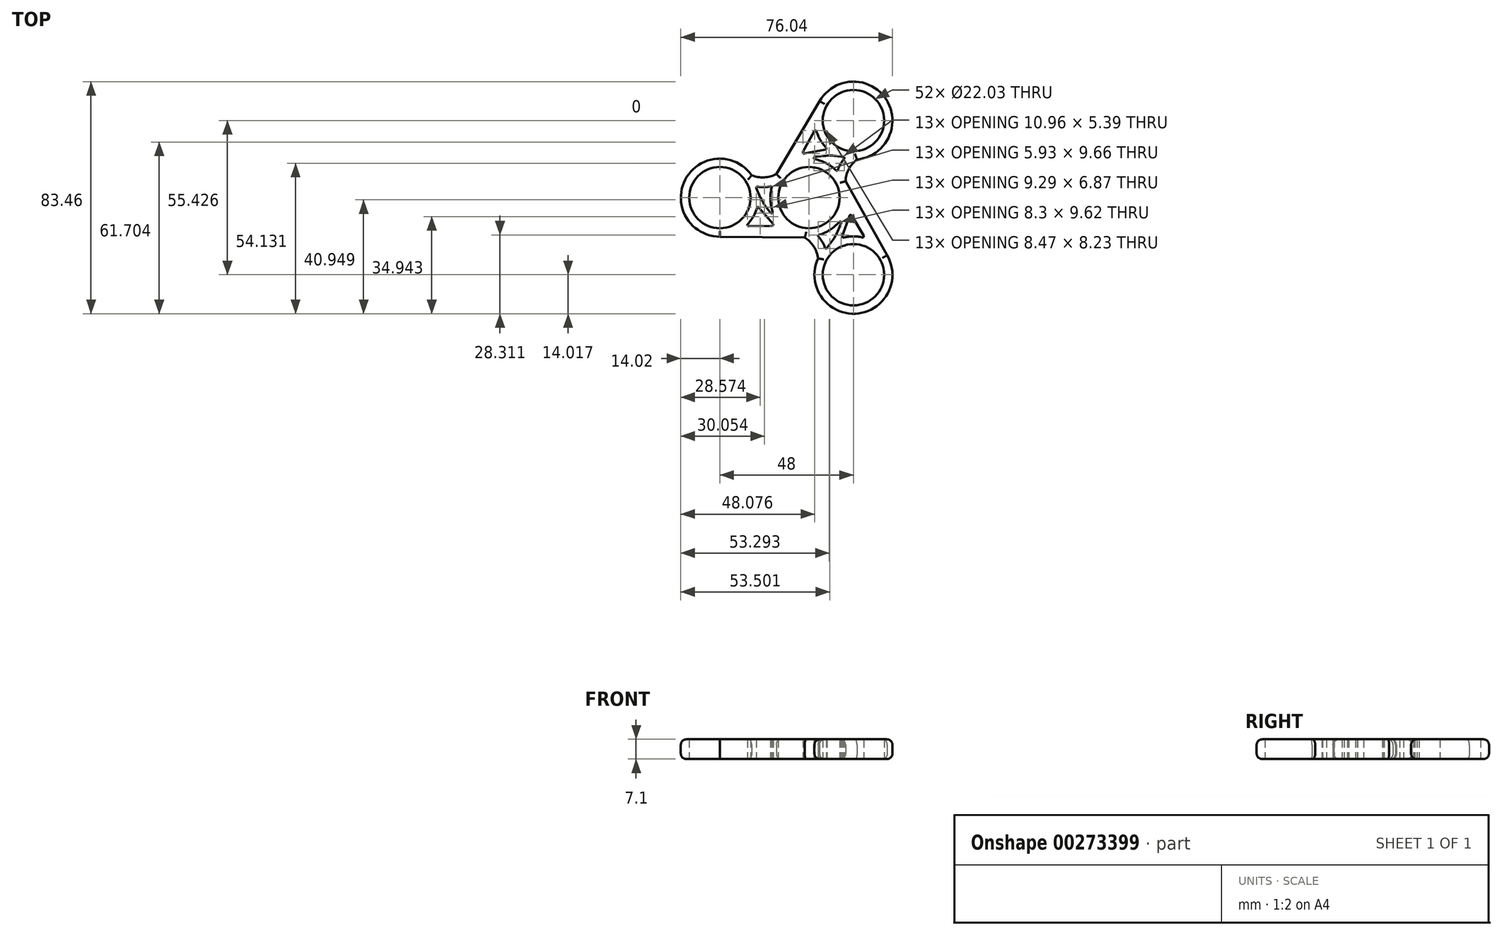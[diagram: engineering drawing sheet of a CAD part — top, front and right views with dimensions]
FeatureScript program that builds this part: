
annotation { "Feature Type Name" : "Feature", "Feature Type Description" : "" }
export const myFeature = defineFeature(function(context is Context, id is Id, definition is map)
    precondition{}
    {
        {
            var Q0;
            Q0=qCreatedBy(makeId("Top.planeOp"),FACE);
            var sketch = newSketch(context, id + "F0", { "sketchPlane" : qUnion([Q0])});
            skCircle(sketch, "E0", {"center": v(0, 0) * mm, "radius": 11.02 * mm});
            skCircle(sketch, "E1", {"center": v(16, 27.71) * mm, "radius": 11.02 * mm});
            skLineSegment(sketch, "E2", {"start": v(0, 0) * mm, "end": v(16, 27.71) * mm, "construction": true});
            skArc(sketch, "E3", {"start": v(17.28, 13.76) * mm, "mid": v(27.8, 35.27) * mm, "end": v(3.86, 34.72) * mm});
            skLineSegment(sketch, "E4", {"start": v(16, 27.71) * mm, "end": v(3.86, 34.72) * mm, "construction": true});
            skPoint(sketch, "E5.visualSharp", {"position": v(9, 15.58) * mm});
            skLineSegment(sketch, "E6", {"start": v(16, 27.71) * mm, "end": v(28.14, 20.7) * mm, "construction": true});
            skArc(sketch, "E7", {"start": v(2.75, 23.79) * mm, "mid": v(4.1, 20.69) * mm, "end": v(6.17, 18) * mm});
            skPoint(sketch, "E8.center", {"position": v(-0.23, 0.06) * mm});
            skLineSegment(sketch, "E9", {"start": v(5.94, 17.3) * mm, "end": v(-1.68, 15.87) * mm});
            skPoint(sketch, "E10.orphan", {"position": v(9.2, 15.94) * mm});
            skPoint(sketch, "E11.1.5", {"position": v(0.06, -0.23) * mm});
            skPoint(sketch, "E11.2.5", {"position": v(0.17, 0.17) * mm});
            skLineSegment(sketch, "E12", {"start": v(1.98, 23.87) * mm, "end": v(-2.13, 16.49) * mm});
            skArc(sketch, "E13", {"start": v(12.66, 13.98) * mm, "mid": v(11.36, 12.1) * mm, "end": v(10.44, 10) * mm});
            skArc(sketch, "E14", {"start": v(9.74, 9.82) * mm, "mid": v(6.22, 12.36) * mm, "end": v(2.13, 13.8) * mm});
            skPoint(sketch, "E15.orphan", {"position": v(2.3, 25.96) * mm});
            skArc(sketch, "E16.filletArc", {"start": v(-2.13, 16.49) * mm, "mid": v(-2.1, 16.03) * mm, "end": v(-1.68, 15.87) * mm});
            skPoint(sketch, "E17.visualSharp", {"position": v(10.24, 9.32) * mm});
            skArc(sketch, "E17.filletArc", {"start": v(9.74, 9.82) * mm, "mid": v(10.14, 9.72) * mm, "end": v(10.44, 10) * mm});
            skPoint(sketch, "E18.visualSharp", {"position": v(13.18, 14.57) * mm});
            skArc(sketch, "E18.filletArc", {"start": v(12.66, 13.98) * mm, "mid": v(12.73, 14.4) * mm, "end": v(12.38, 14.67) * mm});
            skArc(sketch, "E19.filletArc", {"start": v(2.16, 14.64) * mm, "mid": v(1.8, 14.24) * mm, "end": v(2.13, 13.8) * mm});
            skPoint(sketch, "E20.visualSharp", {"position": v(6.76, 17.44) * mm});
            skArc(sketch, "E20.filletArc", {"start": v(5.94, 17.3) * mm, "mid": v(6.27, 17.58) * mm, "end": v(6.17, 18) * mm});
            skPoint(sketch, "E21.visualSharp", {"position": v(2.5, 24.8) * mm});
            skArc(sketch, "E21.filletArc", {"start": v(2.75, 23.79) * mm, "mid": v(2.4, 24.09) * mm, "end": v(1.98, 23.87) * mm});
            skArc(sketch, "E22", {"start": v(12.38, 14.67) * mm, "mid": v(7.27, 15.1) * mm, "end": v(2.16, 14.64) * mm});
            skArc(sketch, "E23", {"start": v(17.28, 13.76) * mm, "mid": v(14.34, 10.27) * mm, "end": v(13.18, 5.86) * mm});
            skLineSegment(sketch, "E24.1.1", {"start": v(-11.67, 8.49) * mm, "end": v(3.86, 34.72) * mm});
            skArc(sketch, "E25.1.0", {"start": v(-20.55, 8.08) * mm, "mid": v(-44.44, 6.45) * mm, "end": v(-32, -14.01) * mm});
            skPoint(sketch, "E25.1.1", {"position": v(-23.63, -11) * mm});
            skPoint(sketch, "E25.1.2", {"position": v(-13.2, 4.2) * mm});
            skLineSegment(sketch, "E25.1.3", {"start": v(-1.51, -14.35) * mm, "end": v(-32, -14.01) * mm});
            skArc(sketch, "E25.1.4", {"start": v(-20.55, 8.08) * mm, "mid": v(-16.06, 7.28) * mm, "end": v(-11.67, 8.49) * mm});
            skCircle(sketch, "E25.1.5", {"center": v(-32, 0) * mm, "radius": 11.02 * mm});
            skPoint(sketch, "E25.1.6", {"position": v(-19.2, 4.13) * mm});
            skPoint(sketch, "E25.1.7", {"position": v(-17.98, 0) * mm});
            skArc(sketch, "E25.1.8", {"start": v(-21.98, -9.5) * mm, "mid": v(-19.97, -6.79) * mm, "end": v(-18.68, -3.66) * mm});
            skLineSegment(sketch, "E25.1.9", {"start": v(-21.66, -10.22) * mm, "end": v(-13.22, -10.09) * mm});
            skArc(sketch, "E25.1.10", {"start": v(-13.38, 3.53) * mm, "mid": v(-13.82, -0.8) * mm, "end": v(-13.02, -5.06) * mm});
            skArc(sketch, "E25.1.11", {"start": v(-18.9, 3.39) * mm, "mid": v(-16.71, -1.25) * mm, "end": v(-13.76, -5.45) * mm});
            skPoint(sketch, "E25.1.12", {"position": v(-18.4, 0) * mm});
            skLineSegment(sketch, "E25.1.13", {"start": v(-17.95, -3.5) * mm, "end": v(-12.9, -9.39) * mm});
            skPoint(sketch, "E25.1.14", {"position": v(-18.49, -2.87) * mm});
            skPoint(sketch, "E25.1.15", {"position": v(-22.73, -10.24) * mm});
            skArc(sketch, "E25.1.16", {"start": v(-18.44, 3.97) * mm, "mid": v(-18.84, 3.82) * mm, "end": v(-18.9, 3.39) * mm});
            skArc(sketch, "E25.1.17", {"start": v(-18.44, 3.97) * mm, "mid": v(-16.15, 3.8) * mm, "end": v(-13.88, 4.04) * mm});
            skArc(sketch, "E25.1.18", {"start": v(-13.22, -10.09) * mm, "mid": v(-12.84, -9.84) * mm, "end": v(-12.9, -9.39) * mm});
            skArc(sketch, "E25.1.19", {"start": v(-21.98, -9.5) * mm, "mid": v(-22.06, -9.97) * mm, "end": v(-21.66, -10.22) * mm});
            skArc(sketch, "E25.1.20", {"start": v(-13.38, 3.53) * mm, "mid": v(-13.48, 3.92) * mm, "end": v(-13.88, 4.04) * mm});
            skArc(sketch, "E25.1.21", {"start": v(-13.76, -5.45) * mm, "mid": v(-13.23, -5.57) * mm, "end": v(-13.02, -5.06) * mm});
            skArc(sketch, "E25.1.22", {"start": v(-17.95, -3.5) * mm, "mid": v(-18.36, -3.36) * mm, "end": v(-18.68, -3.66) * mm});
            skArc(sketch, "E25.2.0", {"start": v(3.28, -21.84) * mm, "mid": v(16.64, -41.71) * mm, "end": v(28.14, -20.7) * mm});
            skPoint(sketch, "E25.2.1", {"position": v(21.34, -14.97) * mm});
            skPoint(sketch, "E25.2.2", {"position": v(2.95, -13.53) * mm});
            skLineSegment(sketch, "E25.2.3", {"start": v(13.18, 5.86) * mm, "end": v(28.14, -20.7) * mm});
            skArc(sketch, "E25.2.4", {"start": v(3.28, -21.84) * mm, "mid": v(1.72, -17.55) * mm, "end": v(-1.51, -14.35) * mm});
            skCircle(sketch, "E25.2.5", {"center": v(16, -27.71) * mm, "radius": 11.02 * mm});
            skPoint(sketch, "E25.2.6", {"position": v(6.03, -18.7) * mm});
            skPoint(sketch, "E25.2.7", {"position": v(9, -15.58) * mm});
            skArc(sketch, "E25.2.8", {"start": v(19.22, -14.28) * mm, "mid": v(15.86, -13.9) * mm, "end": v(12.51, -14.35) * mm});
            skLineSegment(sketch, "E25.2.9", {"start": v(19.68, -13.65) * mm, "end": v(15.34, -6.4) * mm});
            skArc(sketch, "E25.2.10", {"start": v(3.64, -13.35) * mm, "mid": v(7.6, -11.57) * mm, "end": v(10.9, -8.75) * mm});
            skArc(sketch, "E25.2.11", {"start": v(6.52, -18.06) * mm, "mid": v(9.44, -13.85) * mm, "end": v(11.6, -9.2) * mm});
            skPoint(sketch, "E25.2.12", {"position": v(9.2, -15.94) * mm});
            skLineSegment(sketch, "E25.2.13", {"start": v(12, -13.8) * mm, "end": v(14.58, -6.48) * mm});
            skPoint(sketch, "E25.2.14", {"position": v(11.73, -14.57) * mm});
            skPoint(sketch, "E25.2.15", {"position": v(20.23, -14.56) * mm});
            skArc(sketch, "E25.2.16", {"start": v(5.78, -17.95) * mm, "mid": v(6.11, -18.23) * mm, "end": v(6.52, -18.06) * mm});
            skArc(sketch, "E25.2.17", {"start": v(5.78, -17.95) * mm, "mid": v(4.8, -15.88) * mm, "end": v(3.44, -14.04) * mm});
            skArc(sketch, "E25.2.18", {"start": v(15.34, -6.4) * mm, "mid": v(14.94, -6.2) * mm, "end": v(14.58, -6.48) * mm});
            skArc(sketch, "E25.2.19", {"start": v(19.22, -14.28) * mm, "mid": v(19.66, -14.12) * mm, "end": v(19.68, -13.65) * mm});
            skArc(sketch, "E25.2.20", {"start": v(3.64, -13.35) * mm, "mid": v(3.35, -13.64) * mm, "end": v(3.44, -14.04) * mm});
            skArc(sketch, "E25.2.21", {"start": v(11.6, -9.2) * mm, "mid": v(11.43, -8.67) * mm, "end": v(10.9, -8.75) * mm});
            skArc(sketch, "E25.2.22", {"start": v(12, -13.8) * mm, "mid": v(12.1, -14.22) * mm, "end": v(12.51, -14.35) * mm});
            skLineSegment(sketch, "E26", {"start": v(30.02, 27.71) * mm, "end": v(30.02, -27.71) * mm, "construction": true});
            skCircle(sketch, "E27", {"center": v(0, 0) * mm, "radius": 45.81 * mm, "construction": true});
            skSolve(sketch);
        }
        {
            var Q0;
            Q0=makeQuery(id+"F0.imprint","IMPRINT",FACE,{"disambiguationData":[TD([[makeQuery(id+"F0.imprint","IMPRINT",EDGE,{"derivedFrom":sQuery(id+"F0.wireOp",EDGE,"ea44153e-c5e4-4200-878d-53ebf284e07f.1.0")}),-1.0]])]});
            var Q1;
            Q1=makeQuery(id+"F0.imprint","IMPRINT",FACE,{"disambiguationData":[TD([[makeQuery(id+"F0.imprint","IMPRINT",EDGE,{"derivedFrom":sQuery(id+"F0.wireOp",EDGE,"E0")}),-1.0]])]});
            var Q2;
            Q2=makeQuery(id+"F0.imprint","IMPRINT",FACE,{"disambiguationData":[TD([[makeQuery(id+"F0.imprint","IMPRINT",EDGE,{"derivedFrom":sQuery(id+"F0.wireOp",EDGE,"E1")}),-1.0]])]});
            var Q3;
            {var subQ0=sQuery(id+"F0.wireOp",EDGE,"zqQpl2xC-KShR-byGl-JfGq-b1LpVGurQPJH");Q3=makeQuery(id+"F0.imprint","IMPRINT",FACE,{"disambiguationData":[TD([[makeQuery(id+"F0.imprint","IMPRINT",EDGE,{"derivedFrom":subQ0}),-1.0]])]});}
            extrude(context, id + "F1", {"entities" : qUnion([Q0, Q1, Q2, Q3]), "depth" : 7.1 * mm});
        }
        {
            var Q0;
            Q0=makeQuery(id+"F1.opExtrude","CAP_EDGE",EDGE,{"disambiguationData":[OSD([sQuery(id+"F0.wireOp",EDGE,"E25.1.0")])],"isStart":false});
            var Q1;
            Q1=makeQuery(id+"F1.opExtrude","CAP_EDGE",EDGE,{"disambiguationData":[OSD([sQuery(id+"F0.wireOp",EDGE,"E25.1.4")])],"isStart":false});
            var Q2;
            Q2=makeQuery(id+"F1.opExtrude","CAP_EDGE",EDGE,{"disambiguationData":[OSD([sQuery(id+"F0.wireOp",EDGE,"E24.1.1")])],"isStart":false});
            var Q3;
            Q3=makeQuery(id+"F1.opExtrude","CAP_EDGE",EDGE,{"disambiguationData":[OSD([sQuery(id+"F0.wireOp",EDGE,"E3")])],"isStart":false});
            var Q4;
            Q4=makeQuery(id+"F1.opExtrude","CAP_EDGE",EDGE,{"disambiguationData":[OSD([sQuery(id+"F0.wireOp",EDGE,"E23")])],"isStart":false});
            var Q5;
            Q5=makeQuery(id+"F1.opExtrude","CAP_EDGE",EDGE,{"disambiguationData":[OSD([sQuery(id+"F0.wireOp",EDGE,"E25.2.0")])],"isStart":false});
            var Q6;
            Q6=makeQuery(id+"F1.opExtrude","CAP_EDGE",EDGE,{"disambiguationData":[OSD([sQuery(id+"F0.wireOp",EDGE,"E25.2.4")])],"isStart":false});
            var Q7;
            Q7=makeQuery(id+"F1.opExtrude","CAP_EDGE",EDGE,{"disambiguationData":[OSD([sQuery(id+"F0.wireOp",EDGE,"E25.1.3")])],"isStart":false});
            var Q8;
            Q8=makeQuery(id+"F1.opExtrude","CAP_EDGE",EDGE,{"disambiguationData":[OSD([sQuery(id+"F0.wireOp",EDGE,"E25.1.3")])],"isStart":true});
            var Q9;
            Q9=makeQuery(id+"F1.opExtrude","CAP_EDGE",EDGE,{"disambiguationData":[OSD([sQuery(id+"F0.wireOp",EDGE,"E25.2.4")])],"isStart":true});
            var Q10;
            Q10=makeQuery(id+"F1.opExtrude","CAP_EDGE",EDGE,{"disambiguationData":[OSD([sQuery(id+"F0.wireOp",EDGE,"E25.2.0")])],"isStart":true});
            var Q11;
            Q11=makeQuery(id+"F1.opExtrude","CAP_EDGE",EDGE,{"disambiguationData":[OSD([sQuery(id+"F0.wireOp",EDGE,"E25.2.3")])],"isStart":true});
            var Q12;
            Q12=makeQuery(id+"F1.opExtrude","CAP_EDGE",EDGE,{"disambiguationData":[OSD([sQuery(id+"F0.wireOp",EDGE,"E23")])],"isStart":true});
            var Q13;
            Q13=makeQuery(id+"F1.opExtrude","CAP_EDGE",EDGE,{"disambiguationData":[OSD([sQuery(id+"F0.wireOp",EDGE,"E25.1.0")])],"isStart":true});
            var Q14;
            Q14=makeQuery(id+"F1.opExtrude","CAP_EDGE",EDGE,{"disambiguationData":[OSD([sQuery(id+"F0.wireOp",EDGE,"E25.1.4")])],"isStart":true});
            var Q15;
            Q15=makeQuery(id+"F1.opExtrude","CAP_EDGE",EDGE,{"disambiguationData":[OSD([sQuery(id+"F0.wireOp",EDGE,"E24.1.1")])],"isStart":true});
            var Q16;
            Q16=makeQuery(id+"F1.opExtrude","CAP_EDGE",EDGE,{"disambiguationData":[OSD([sQuery(id+"F0.wireOp",EDGE,"E3")])],"isStart":true});
            fillet(context, id + "F2", {"entities" : qUnion([Q0, Q1, Q2, Q3, Q4, Q5, Q6, Q7, Q8, Q9, Q10, Q11, Q12, Q13, Q14, Q15, Q16]), "radius" : 2 * mm, "tangentPropagation" : true, "allowEdgeOverflow" : false});
        }
    });
